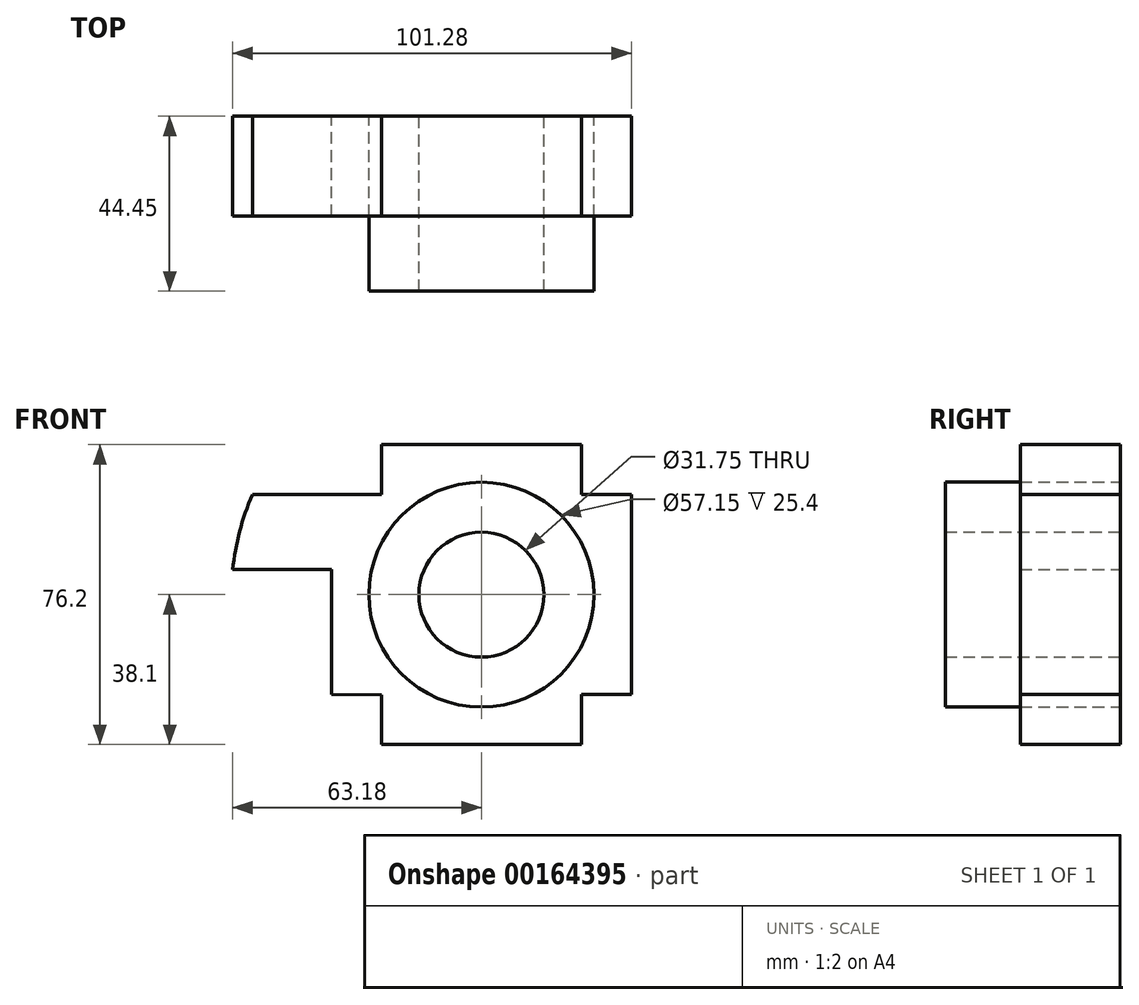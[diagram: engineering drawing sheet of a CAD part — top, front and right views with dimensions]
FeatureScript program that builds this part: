
annotation { "Feature Type Name" : "Feature", "Feature Type Description" : "" }
export const myFeature = defineFeature(function(context is Context, id is Id, definition is map)
    precondition{}
    {
        {
            var Q0;
            Q0=qCreatedBy(makeId("Front.planeOp"),FACE);
            var sketch = newSketch(context, id + "F0", { "sketchPlane" : qUnion([Q0])});
            skCircle(sketch, "E0", {"center": v(0, 0) * mm, "radius": 15.88 * mm});
            skCircle(sketch, "E1", {"center": v(0, 0) * mm, "radius": 28.58 * mm});
            skLineSegment(sketch, "E2.bottom", {"start": v(38.1, 38.1) * mm, "end": v(-38.1, 38.1) * mm});
            skLineSegment(sketch, "E2.top", {"start": v(38.1, -38.1) * mm, "end": v(-38.1, -38.1) * mm});
            skLineSegment(sketch, "E2.left", {"start": v(38.1, 38.1) * mm, "end": v(38.1, -38.1) * mm});
            skLineSegment(sketch, "E2.right", {"start": v(-38.1, 38.1) * mm, "end": v(-38.1, -38.1) * mm});
            skLineSegment(sketch, "E3", {"start": v(38.1, 25.4) * mm, "end": v(38.1, -50.8) * mm});
            skLineSegment(sketch, "E4", {"start": v(38.1, 25.4) * mm, "end": v(38.1, 6.35) * mm});
            skCircle(sketch, "E5", {"center": v(0, 0) * mm, "radius": 63.5 * mm});
            skLineSegment(sketch, "E6", {"start": v(38.1, -50.8) * mm, "end": v(38.1, -50.8) * mm});
            skLineSegment(sketch, "E7", {"start": v(38.1, 25.4) * mm, "end": v(58.2, 25.4) * mm});
            skLineSegment(sketch, "E8", {"start": v(38.1, 6.35) * mm, "end": v(63.18, 6.35) * mm});
            skLineSegment(sketch, "E9", {"start": v(25.4, 38.1) * mm, "end": v(6.35, 38.1) * mm});
            skLineSegment(sketch, "E10", {"start": v(-25.4, 38.1) * mm, "end": v(-6.35, 38.1) * mm});
            skLineSegment(sketch, "E11", {"start": v(-38.1, 25.4) * mm, "end": v(-38.1, 13.66) * mm});
            skLineSegment(sketch, "E12", {"start": v(-38.1, -25.4) * mm, "end": v(-38.1, 50.8) * mm});
            skLineSegment(sketch, "E13", {"start": v(-25.4, -38.1) * mm, "end": v(-6.35, -38.1) * mm});
            skLineSegment(sketch, "E14", {"start": v(25.4, -38.1) * mm, "end": v(6.35, -38.1) * mm});
            skLineSegment(sketch, "E15", {"start": v(25.4, -38.1) * mm, "end": v(25.4, -58.2) * mm});
            skLineSegment(sketch, "E16", {"start": v(6.35, -38.1) * mm, "end": v(6.35, -63.18) * mm});
            skLineSegment(sketch, "E17", {"start": v(-6.35, -38.1) * mm, "end": v(-6.35, -63.18) * mm});
            skLineSegment(sketch, "E18", {"start": v(-25.4, -38.1) * mm, "end": v(-25.4, -58.2) * mm});
            skLineSegment(sketch, "E19", {"start": v(-38.1, -25.4) * mm, "end": v(-38.1, -6.35) * mm});
            skLineSegment(sketch, "E20", {"start": v(-38.1, -25.4) * mm, "end": v(-58.2, -25.4) * mm});
            skLineSegment(sketch, "E21", {"start": v(-38.1, -6.35) * mm, "end": v(-63.18, -6.35) * mm});
            skLineSegment(sketch, "E22", {"start": v(-38.1, 25.4) * mm, "end": v(-58.2, 25.4) * mm});
            skLineSegment(sketch, "E23", {"start": v(25.4, 38.1) * mm, "end": v(25.4, 58.2) * mm});
            skLineSegment(sketch, "E24", {"start": v(6.35, 38.1) * mm, "end": v(6.35, 63.18) * mm});
            skLineSegment(sketch, "E25", {"start": v(-6.35, 38.1) * mm, "end": v(-6.35, 63.18) * mm});
            skLineSegment(sketch, "E26", {"start": v(-25.4, 38.1) * mm, "end": v(-25.4, 58.2) * mm});
            skLineSegment(sketch, "E27", {"start": v(38.1, -25.4) * mm, "end": v(38.1, -6.35) * mm});
            skLineSegment(sketch, "E28", {"start": v(38.1, -25.4) * mm, "end": v(58.2, -25.4) * mm});
            skLineSegment(sketch, "E29", {"start": v(38.1, -6.35) * mm, "end": v(63.18, -6.35) * mm});
            skLineSegment(sketch, "E30", {"start": v(38.1, 25.4) * mm, "end": v(25.4, 25.4) * mm});
            skLineSegment(sketch, "E31", {"start": v(25.4, 25.4) * mm, "end": v(25.4, 38.1) * mm});
            skLineSegment(sketch, "E32", {"start": v(-25.4, 38.1) * mm, "end": v(-25.4, 25.4) * mm});
            skLineSegment(sketch, "E33", {"start": v(-25.4, 25.4) * mm, "end": v(-38.1, 25.4) * mm});
            skLineSegment(sketch, "E34", {"start": v(-25.4, -38.1) * mm, "end": v(-25.4, -25.44) * mm});
            skLineSegment(sketch, "E35", {"start": v(-25.4, -25.44) * mm, "end": v(-38.1, -25.4) * mm});
            skLineSegment(sketch, "E36", {"start": v(25.4, -38.1) * mm, "end": v(25.4, -25.4) * mm});
            skLineSegment(sketch, "E37", {"start": v(25.4, -25.4) * mm, "end": v(38.1, -25.4) * mm});
            skLineSegment(sketch, "E38", {"start": v(-38.1, 25.4) * mm, "end": v(-38.1, 6.35) * mm});
            skLineSegment(sketch, "E39", {"start": v(-38.1, 6.35) * mm, "end": v(-63.18, 6.35) * mm});
            skSolve(sketch);
        }
        {
            var Q0;
            Q0=makeQuery(id+"F0.imprint","IMPRINT",FACE,{"disambiguationData":[TD([[makeQuery(id+"F0.imprint","IMPRINT",EDGE,{"derivedFrom":sQuery(id+"F0.wireOp",EDGE,"E4")}),1.0]])]});
            var Q1;
            Q1=makeQuery(id+"F0.imprint","IMPRINT",FACE,{"disambiguationData":[TD([[makeQuery(id+"F0.imprint","IMPRINT",EDGE,{"derivedFrom":sQuery(id+"F0.wireOp",EDGE,"E27")}),-1.0]])]});
            var Q2;
            Q2=makeQuery(id+"F0.imprint","IMPRINT",FACE,{"disambiguationData":[TD([[makeQuery(id+"F0.imprint","IMPRINT",EDGE,{"derivedFrom":sQuery(id+"F0.wireOp",EDGE,"E14")}),1.0]])]});
            var Q3;
            Q3=makeQuery(id+"F0.imprint","IMPRINT",FACE,{"disambiguationData":[TD([[makeQuery(id+"F0.imprint","IMPRINT",EDGE,{"derivedFrom":sQuery(id+"F0.wireOp",EDGE,"E13")}),-1.0]])]});
            var Q4;
            Q4=makeQuery(id+"F0.imprint","IMPRINT",FACE,{"disambiguationData":[TD([[makeQuery(id+"F0.imprint","IMPRINT",EDGE,{"derivedFrom":sQuery(id+"F0.wireOp",EDGE,"E19")}),1.0]])]});
            var Q5;
            {var subQ0=sQuery(id+"F0.wireOp",EDGE,"RUIVs9Zc-yXI2-jfIG-2WZB-j2fVre0khlyT");Q5=makeQuery(id+"F0.imprint","IMPRINT",FACE,{"disambiguationData":[TD([[makeQuery(id+"F0.imprint","IMPRINT",EDGE,{"derivedFrom":subQ0}),-1.0]])]});}
            var Q6;
            Q6=makeQuery(id+"F0.imprint","IMPRINT",FACE,{"disambiguationData":[TD([[makeQuery(id+"F0.imprint","IMPRINT",EDGE,{"derivedFrom":sQuery(id+"F0.wireOp",EDGE,"E9")}),-1.0]])]});
            var Q7;
            Q7=makeQuery(id+"F0.imprint","IMPRINT",FACE,{"disambiguationData":[TD([[makeQuery(id+"F0.imprint","IMPRINT",EDGE,{"derivedFrom":sQuery(id+"F0.wireOp",EDGE,"E10")}),1.0]])]});
            var Q8;
            Q8=makeQuery(id+"F0.imprint","IMPRINT",FACE,{"disambiguationData":[TD([[makeQuery(id+"F0.imprint","IMPRINT",EDGE,{"derivedFrom":sQuery(id+"F0.wireOp",EDGE,"E1")}),-1.0]])]});
            var Q9;
            {var subQ0=sQuery(id+"F0.wireOp",EDGE,"E22");Q9=makeQuery(id+"F0.imprint","IMPRINT",FACE,{"disambiguationData":[TD([[makeQuery(id+"F0.imprint","IMPRINT",EDGE,{"derivedFrom":subQ0}),1.0]])]});}
            extrude(context, id + "F1", {"entities" : qUnion([Q0, Q1, Q2, Q3, Q4, Q5, Q6, Q7, Q8, Q9]), "depth" : 25.4 * mm});
        }
        {
            var Q0;
            Q0=makeQuery(id+"F0.imprint","IMPRINT",FACE,{"disambiguationData":[TD([[makeQuery(id+"F0.imprint","IMPRINT",EDGE,{"derivedFrom":sQuery(id+"F0.wireOp",EDGE,"E0")}),-1.0]])]});
            extrude(context, id + "F2", {"entities" : qUnion([Q0]), "depth" : 44.45 * mm});
        }
    });
